# Revit family: RUFO-490-3750-830x
name_source: partatom
category: Oprawy oświetleniowe
revit_build: Autodesk Revit 2017 (Build: 20190507_1515(x64)
units: mm (PartAtom-declared; Revit-internal decimal feet)

## family parameters
Numer OmniClass = 23.80.70.11
Obiekt nadrzędny = Powierzchnia
Punkt obliczania pomieszczeń = Nie
Tnij formami wycięć po wczytaniu = Tak
Typ części = Normalny
Tytuł OmniClass = Luminaries for Internal Lighting
Współdzielony = Nie
Wymiar okrągłego złącza = Użyj średnicy
Źródło światła = Tak

## types (10) — shared parameters
Emituj kształt widoczny w renderingu = Nie
Emituj ze średnicy okręgu = 490 mm  [stored 1.60761 ft]
Filtr koloru = 16777215
Kod zespołu = D5020200
Lampa = LED
Obciążenie pozorne = 28 VA
Odchylenie kierunku = 90.00°
Plik sieci fotometrycznej = RUFO 4903750-840.IES
Producent = RIDI Leuchten GmbH
URL = www.ridi.de
Zmiana temperatury barwowej przyciemniania lampy = <Brak>
brand = RIDI
conformity mark = CE
electrical safety class = 1
height = 145 mm  [stored 0.475722 ft]
ingress protection (IP) code = IP20
length = 490 mm  [stored 1.60761 ft]
nominal frequency = 50-60Hz
nominal voltage = 230
rated input power = 28
voltage type (AC, DC, UC) = AC
width = 490 mm  [stored 1.60761 ft]
zero-valued in all types: Domyślna rzędna

## per-type parameters (varying)
| type | Model | product name | weight |
| RUFO 490/3750-830 | 0420734 | RUFO 490/3750-830 | 2.1kg |
| RUFO 490/3750-830-DALI | 0430734 | RUFO 490/3750-830-DALI | 2.1kg |
| RUFO 490/3750-830 2K | 0420735 | RUFO 490/3750-830 2K | 2.1kg |
| RUFO 490/3750-830 2K-DALI | 0430735 | RUFO 490/3750-830 2K-DALI | 2.1kg |
| RUFO 490/3750-830 2K-EDS3 | 0420735//377 | RUFO 490/3750-830 2K-DALI | 2.1kg |
| RUFO 490/3750-830 2K-RS | 0420735//396 | RUFO 490/3750-830 2K-RS | 2.1kg |
| RUFO 490/3750-830 2K-RS-EDS3 | 0420735//377396 | RUFO 490/3750-830 2K-RS-EDS3 | 2.1kg |
| RUFO 490/3750-830 EDS3 | 0420734//377 | RUFO 490/3750-830 EDS3 | 2.5kg |
| RUFO 490/3750-830 EDS3-DALI | 0430734//377 | RUFO 490/3750-830 EDS3-DALI | 2.1kg |
| RUFO 490/3750-830 RS-EDS3 | 0420734//377396 | RUFO 490/3750-830 RS-EDS3 | 2.1kg |

note: [stored X ft] marks values corroborated as IEEE doubles in the binary element streams (Revit-internal decimal feet)
